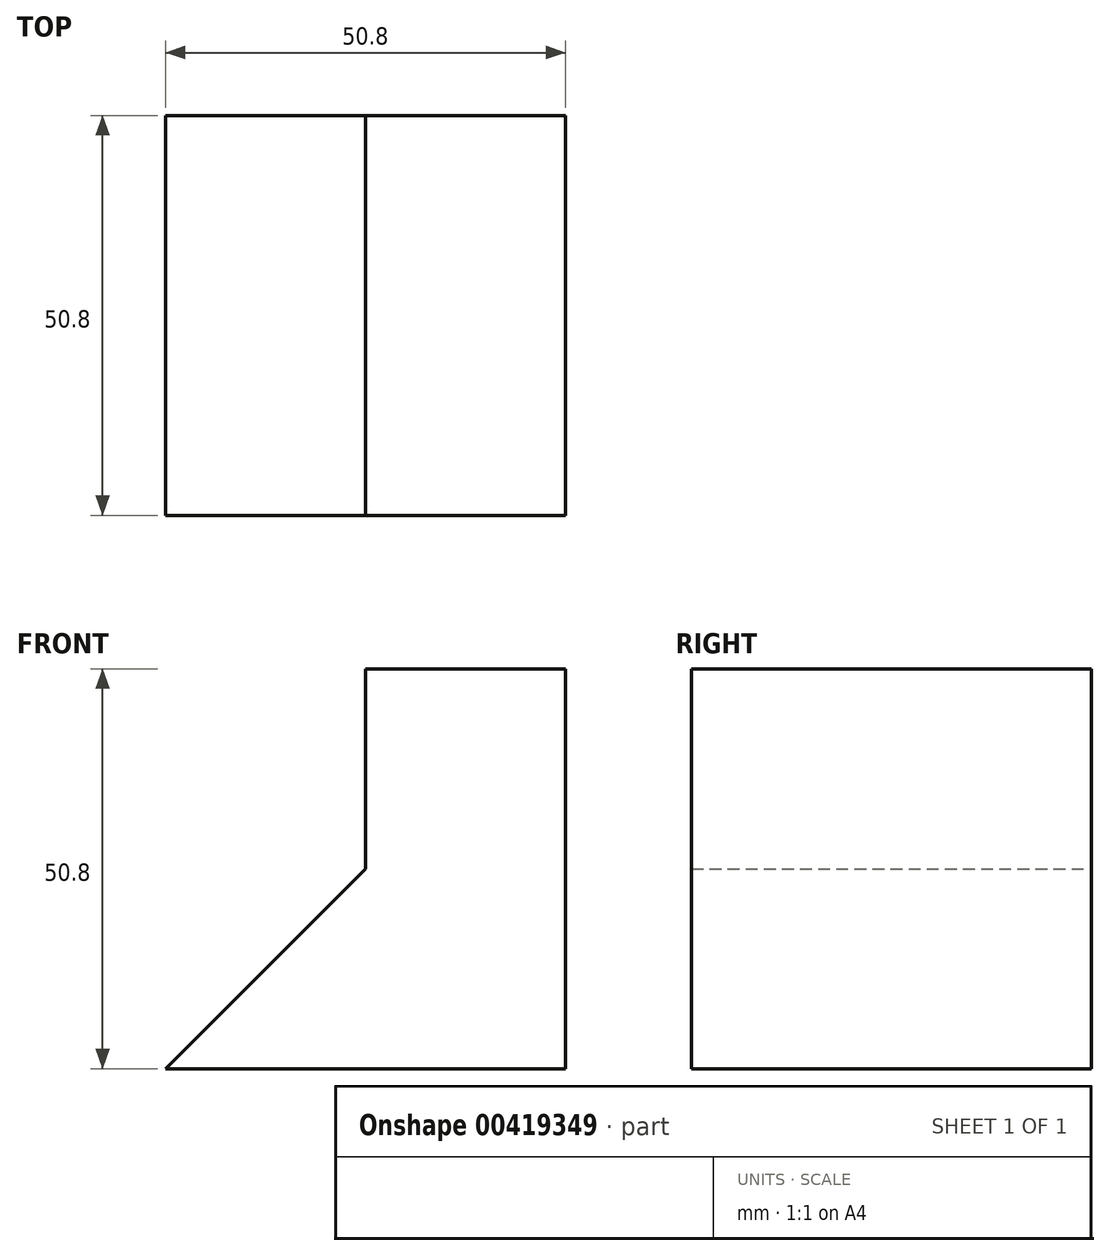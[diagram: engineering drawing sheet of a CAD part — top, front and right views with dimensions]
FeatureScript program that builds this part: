
annotation { "Feature Type Name" : "Feature", "Feature Type Description" : "" }
export const myFeature = defineFeature(function(context is Context, id is Id, definition is map)
    precondition{}
    {
        {
            var Q0;
            Q0=qCreatedBy(makeId("Front.planeOp"),FACE);
            var sketch = newSketch(context, id + "F0", { "sketchPlane" : qUnion([Q0])});
            skLineSegment(sketch, "E0", {"start": v(-30.17, -41.82) * mm, "end": v(20.63, -41.82) * mm});
            skLineSegment(sketch, "E1", {"start": v(20.63, -41.82) * mm, "end": v(20.63, 8.98) * mm});
            skLineSegment(sketch, "E2", {"start": v(20.63, 8.98) * mm, "end": v(-4.77, 8.98) * mm});
            skLineSegment(sketch, "E3", {"start": v(-4.77, 8.98) * mm, "end": v(-4.77, -16.42) * mm});
            skLineSegment(sketch, "E4", {"start": v(-4.77, -16.42) * mm, "end": v(-30.17, -41.82) * mm});
            skSolve(sketch);
        }
        {
            var Q0;
            Q0 = qSketchRegion(id + "F0", true);
            extrude(context, id + "F1", {"entities" : qUnion([Q0]), "depth" : 50.8 * mm});
        }
    });
